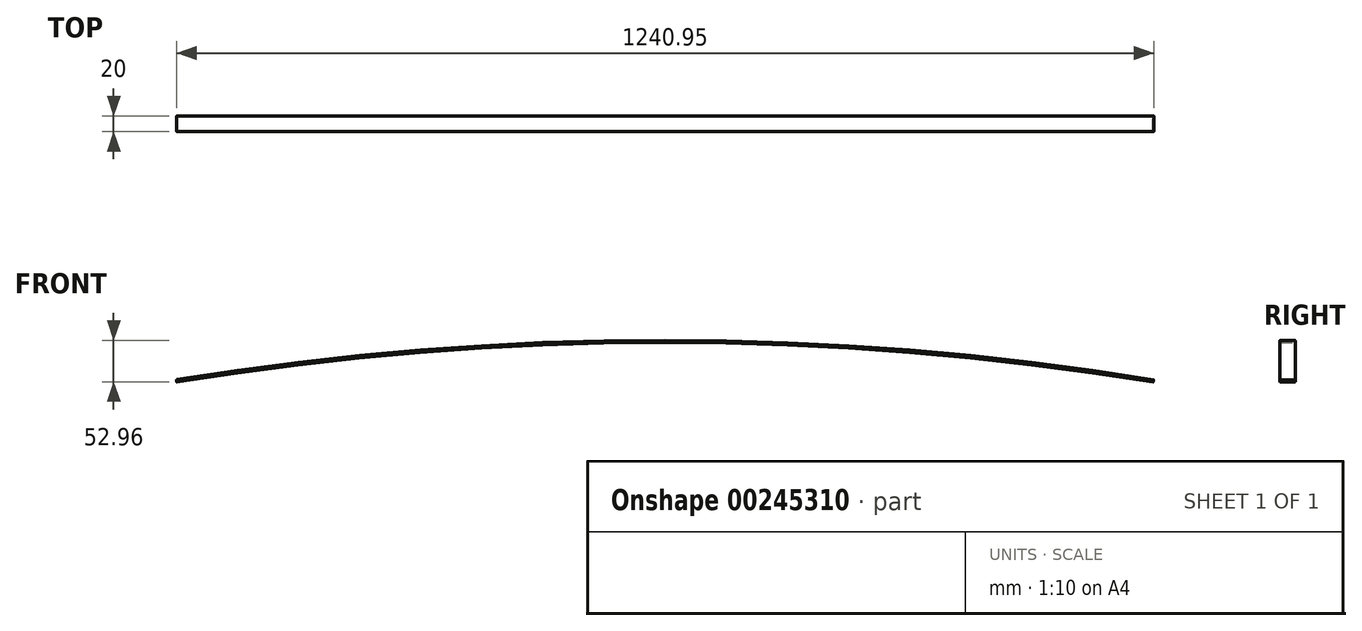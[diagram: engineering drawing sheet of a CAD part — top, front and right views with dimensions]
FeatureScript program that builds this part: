
annotation { "Feature Type Name" : "Feature", "Feature Type Description" : "" }
export const myFeature = defineFeature(function(context is Context, id is Id, definition is map)
    precondition{}
    {
        {
            var Q0;
            Q0=qCreatedBy(makeId("Front.planeOp"),FACE);
            var sketch = newSketch(context, id + "F0", { "sketchPlane" : qUnion([Q0])});
            skLineSegment(sketch, "E0", {"start": v(0, 40) * mm, "end": v(0, -40) * mm, "construction": true});
            skLineSegment(sketch, "E1", {"start": v(0, 0) * mm, "end": v(1240, 0) * mm, "construction": true});
            skLineSegment(sketch, "E2", {"start": v(1240, 40) * mm, "end": v(1240, -40) * mm, "construction": true});
            skLineSegment(sketch, "E3", {"start": v(620, 90) * mm, "end": v(620, -90) * mm, "construction": true});
            skPoint(sketch, "E3.startSnap0", {"position": v(620, 0) * mm});
            skArc(sketch, "E4", {"start": v(1240, 40) * mm, "mid": v(620, 90) * mm, "end": v(0, 40) * mm});
            skArc(sketch, "E5", {"start": v(0, -40) * mm, "mid": v(620, -90) * mm, "end": v(1240, -40) * mm});
            skSolve(sketch);
        }
        {
            var Q0;
            Q0=qCreatedBy(makeId("Right.planeOp"),FACE);
            var sketch = newSketch(context, id + "F1", { "sketchPlane" : qUnion([Q0])});
            skLineSegment(sketch, "E6.bottom", {"start": v(-6.28, 40) * mm, "end": v(11.72, 40) * mm});
            skLineSegment(sketch, "E6.top", {"start": v(-6.28, 43) * mm, "end": v(11.72, 43) * mm});
            skLineSegment(sketch, "E6.left", {"start": v(-7.28, 41) * mm, "end": v(-7.28, 42) * mm});
            skLineSegment(sketch, "E6.right", {"start": v(12.72, 41) * mm, "end": v(12.72, 42) * mm});
            skPoint(sketch, "E7.visualSharp", {"position": v(-7.28, 43) * mm});
            skArc(sketch, "E7.filletArc", {"start": v(-6.28, 43) * mm, "mid": v(-7, 42.7) * mm, "end": v(-7.28, 42) * mm});
            skPoint(sketch, "E8.visualSharp", {"position": v(-7.28, 40) * mm});
            skArc(sketch, "E8.filletArc", {"start": v(-7.28, 41) * mm, "mid": v(-7, 40.3) * mm, "end": v(-6.28, 40) * mm});
            skPoint(sketch, "E9.visualSharp", {"position": v(12.72, 40) * mm});
            skArc(sketch, "E9.filletArc", {"start": v(11.72, 40) * mm, "mid": v(12.42, 40.3) * mm, "end": v(12.72, 41) * mm});
            skPoint(sketch, "E10.visualSharp", {"position": v(12.72, 43) * mm});
            skArc(sketch, "E10.filletArc", {"start": v(12.72, 42) * mm, "mid": v(12.42, 42.7) * mm, "end": v(11.72, 43) * mm});
            skSolve(sketch);
        }
        {
            var Q0;
            Q0=makeQuery(id+"F1.imprint","IMPRINT",FACE,{"disambiguationData":[TD([[makeQuery(id+"F1.imprint","IMPRINT",EDGE,{"derivedFrom":sQuery(id+"F1.wireOp",EDGE,"E6.bottom")}),1.0]])]});
            var Q1;
            Q1=sQuery(id+"F1.wireOp",EDGE,"E10.filletArc");
            var Q2;
            Q2=sQuery(id+"F1.wireOp",EDGE,"E9.filletArc");
            var Q3;
            Q3=sQuery(id+"F1.wireOp",EDGE,"E6.right");
            var Q4;
            Q4=sQuery(id+"F1.wireOp",EDGE,"E6.top");
            var Q5;
            Q5=sQuery(id+"F1.wireOp",EDGE,"E6.bottom");
            var Q6;
            Q6=sQuery(id+"F1.wireOp",EDGE,"E8.filletArc");
            var Q7;
            Q7=sQuery(id+"F1.wireOp",EDGE,"E7.filletArc");
            var Q8;
            Q8=sQuery(id+"F1.wireOp",EDGE,"E6.left");
            var Q9;
            Q9=sQuery(id+"F0.wireOp",EDGE,"E4");
            sweep(context, id + "F2", {"profiles" : qUnion([Q0]), "surfaceProfiles" : qUnion([Q1, Q2, Q3, Q4, Q5, Q6, Q7, Q8]), "path" : qUnion([Q9])});
        }
    });
